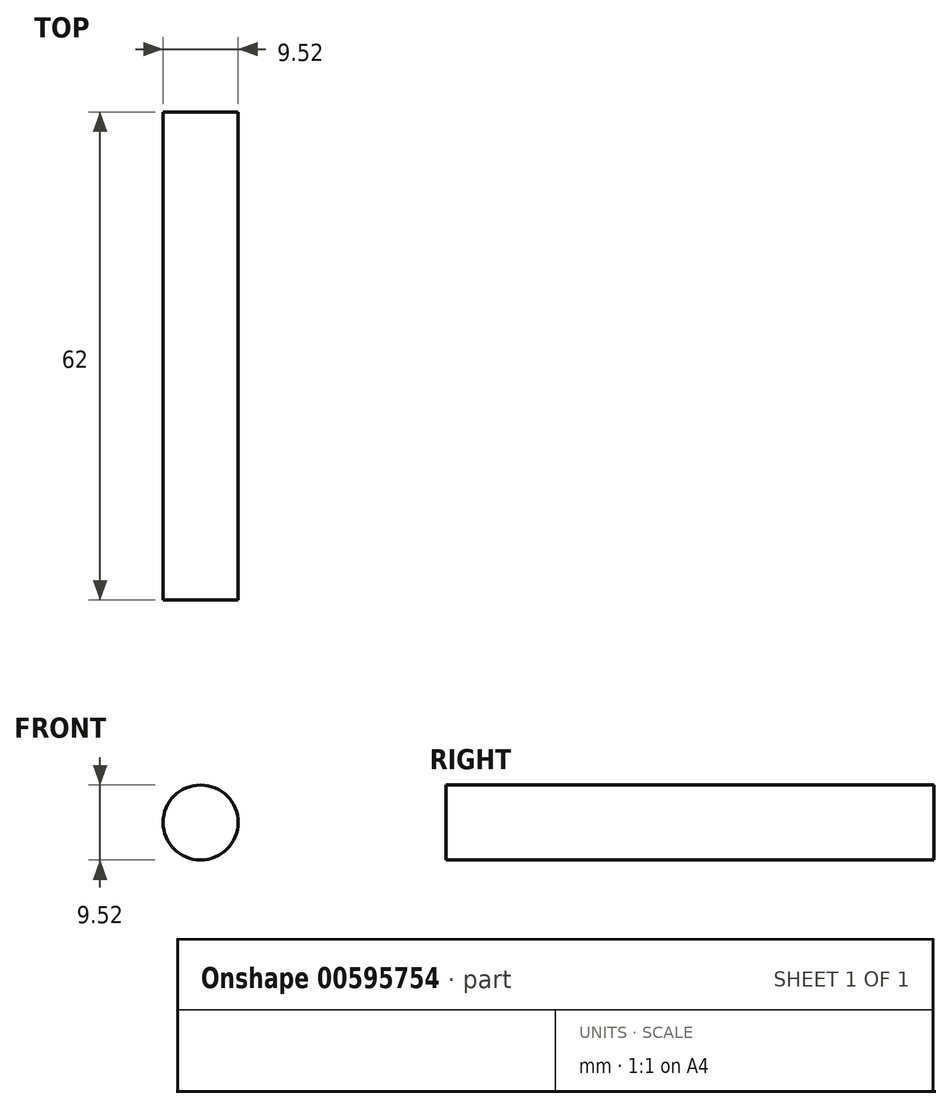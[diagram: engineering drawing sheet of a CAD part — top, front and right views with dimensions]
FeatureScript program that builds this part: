
annotation { "Feature Type Name" : "Feature", "Feature Type Description" : "" }
export const myFeature = defineFeature(function(context is Context, id is Id, definition is map)
    precondition{}
    {
        {
            var Q0;
            Q0=qCreatedBy(makeId("Front.planeOp"),FACE);
            var sketch = newSketch(context, id + "F0", { "sketchPlane" : qUnion([Q0])});
            skCircle(sketch, "E0", {"center": v(0, 0) * mm, "radius": 4.76 * mm});
            skSolve(sketch);
        }
        {
            var Q0;
            Q0=makeQuery(id+"F0.imprint","IMPRINT",FACE,{"disambiguationData":[TD([[makeQuery(id+"F0.imprint","IMPRINT",EDGE,{"derivedFrom":sQuery(id+"F0.wireOp",EDGE,"E0")}),1.0]])]});
            extrude(context, id + "F1", {"entities" : qUnion([Q0]), "depth" : 62 * mm, "offsetDistance" : 25 * mm, "symmetric" : true});
        }
    });
